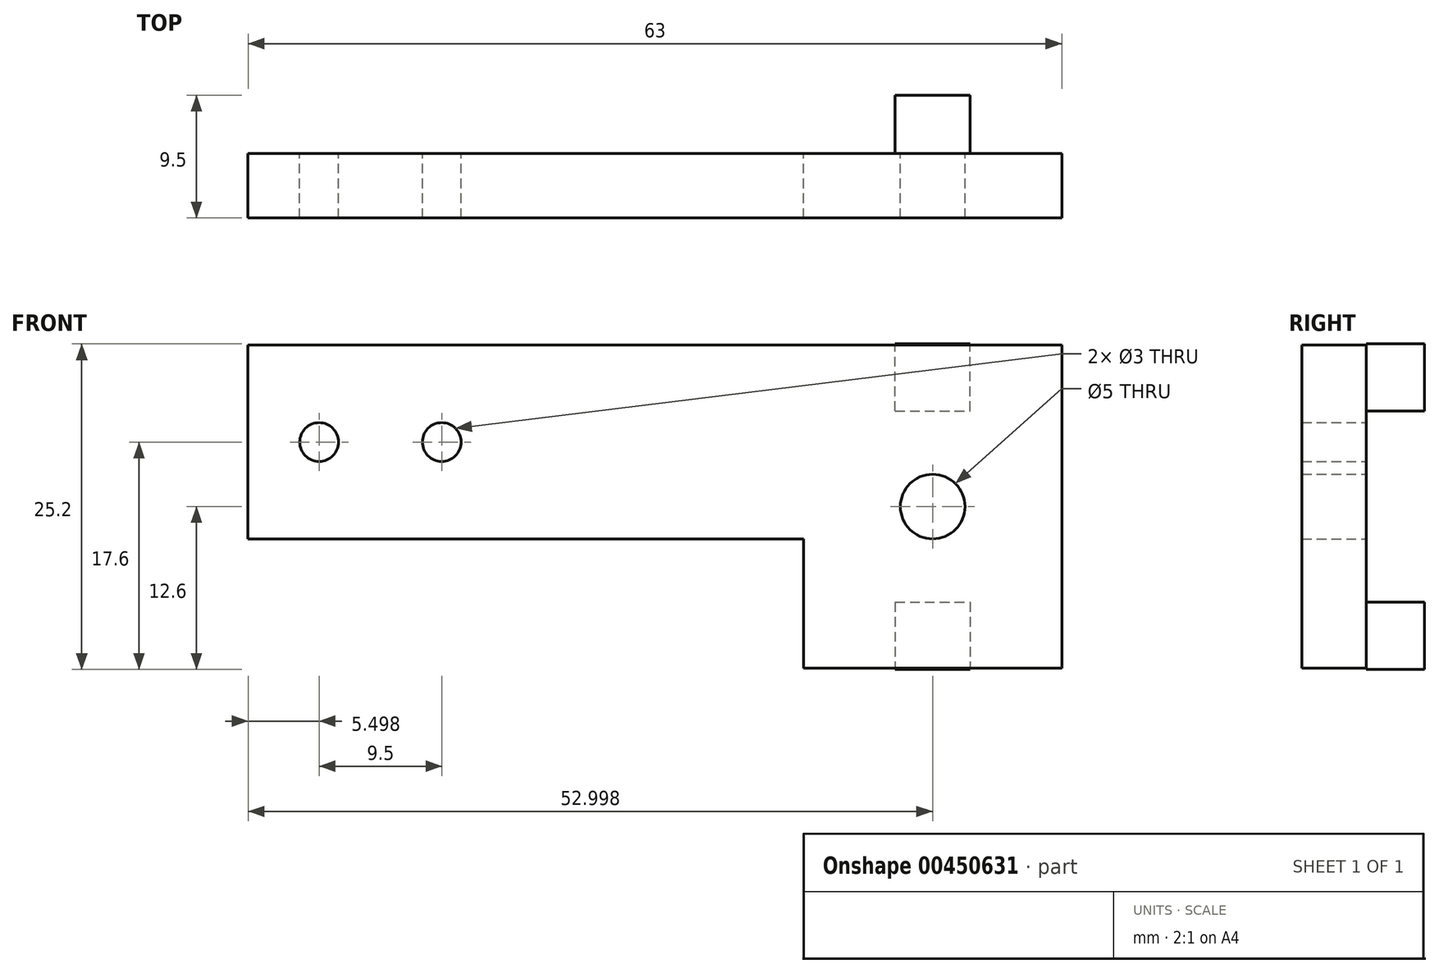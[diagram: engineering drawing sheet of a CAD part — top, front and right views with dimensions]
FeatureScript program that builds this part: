
annotation { "Feature Type Name" : "Feature", "Feature Type Description" : "" }
export const myFeature = defineFeature(function(context is Context, id is Id, definition is map)
    precondition{}
    {
        {
            var Q0;
            Q0=qCreatedBy(makeId("Front.planeOp"),FACE);
            var sketch = newSketch(context, id + "F0", { "sketchPlane" : qUnion([Q0])});
            skLineSegment(sketch, "E0.bottom", {"start": v(34.4, 12.5) * mm, "end": v(14.4, 12.5) * mm});
            skLineSegment(sketch, "E0.top", {"start": v(34.4, -12.5) * mm, "end": v(14.4, -12.5) * mm});
            skLineSegment(sketch, "E0.left", {"start": v(34.4, 12.5) * mm, "end": v(34.4, -12.5) * mm});
            skLineSegment(sketch, "E0.right", {"start": v(14.4, -2.5) * mm, "end": v(14.4, -12.5) * mm});
            skPoint(sketch, "E0.middle", {"position": v(24.4, 0) * mm});
            skLineSegment(sketch, "E1", {"start": v(14.4, 12.5) * mm, "end": v(-28.6, 12.5) * mm});
            skLineSegment(sketch, "E2", {"start": v(14.4, -2.5) * mm, "end": v(-28.6, -2.5) * mm});
            skLineSegment(sketch, "E3", {"start": v(-28.6, 12.5) * mm, "end": v(-28.6, -2.5) * mm});
            skCircle(sketch, "E4", {"center": v(24.4, 0) * mm, "radius": 2.5 * mm});
            skLineSegment(sketch, "E5", {"start": v(-28.6, 5) * mm, "end": v(-6.2, 5) * mm, "construction": true});
            skCircle(sketch, "E6", {"center": v(-13.6, 5) * mm, "radius": 1.5 * mm});
            skPoint(sketch, "E7", {"position": v(-23.1, 12.5) * mm});
            skPoint(sketch, "E8", {"position": v(-28.6, 12.5) * mm});
            skCircle(sketch, "E9", {"center": v(-23.1, 5) * mm, "radius": 1.5 * mm});
            skSolve(sketch);
        }
        {
            var Q0;
            Q0 = qSketchRegion(id + "F0", true);
            extrude(context, id + "F1", {"entities" : qUnion([Q0]), "depth" : 5 * mm});
        }
        {
            var Q0;
            Q0=makeQuery(id+"F1.opExtrude","CAP_FACE",FACE,{"disambiguationData":[OSD([sQuery(id+"F0.wireOp",EDGE,"E0.bottom"),sQuery(id+"F0.wireOp",EDGE,"E0.top"),sQuery(id+"F0.wireOp",EDGE,"E0.left"),sQuery(id+"F0.wireOp",EDGE,"E0.right"),sQuery(id+"F0.wireOp",EDGE,"E1"),sQuery(id+"F0.wireOp",EDGE,"E2"),sQuery(id+"F0.wireOp",EDGE,"E3"),sQuery(id+"F0.wireOp",EDGE,"E4"),sQuery(id+"F0.wireOp",EDGE,"E6"),sQuery(id+"F0.wireOp",EDGE,"E9")])],"isStart":true});
            cPlane(context, id + "F2", {"entities" : qUnion([Q0]), "cplaneType" : CPlaneType.OFFSET, "offset" : 0 * mm, "width" : 150 * mm, "height" : 150 * mm});
        }
        {
            var Q0;
            Q0=qCreatedBy(id+"F2.planeOp",FACE);
            var sketch = newSketch(context, id + "F3", { "sketchPlane" : qUnion([Q0])});
            skCircle(sketch, "E10.0", {"center": v(-24.4, 0) * mm, "radius": 2.5 * mm, "construction": true});
            skLineSegment(sketch, "E11", {"start": v(-24.4, 12.6) * mm, "end": v(-24.4, -13.63) * mm, "construction": true});
            skLineSegment(sketch, "E12.bottom", {"start": v(-21.5, 7.4) * mm, "end": v(-27.3, 7.4) * mm});
            skLineSegment(sketch, "E12.left", {"start": v(-21.5, 7.4) * mm, "end": v(-21.5, 12.6) * mm});
            skLineSegment(sketch, "E12.right", {"start": v(-27.3, 7.4) * mm, "end": v(-27.3, 12.6) * mm});
            skPoint(sketch, "E13", {"position": v(-21.5, 12.6) * mm});
            skPoint(sketch, "E14", {"position": v(-27.3, 12.6) * mm});
            skLineSegment(sketch, "E15", {"start": v(-21.5, 12.6) * mm, "end": v(-27.3, 12.6) * mm});
            skLineSegment(sketch, "E16", {"start": v(-3.15, 0) * mm, "end": v(-41.19, 0) * mm, "construction": true});
            skLineSegment(sketch, "E17.MirrorCS", {"start": v(-21.5, -7.4) * mm, "end": v(-21.5, -12.6) * mm});
            skLineSegment(sketch, "E18.MirrorCS", {"start": v(-21.5, -12.6) * mm, "end": v(-27.3, -12.6) * mm});
            skLineSegment(sketch, "E19.MirrorCS", {"start": v(-27.3, -7.4) * mm, "end": v(-27.3, -12.6) * mm});
            skLineSegment(sketch, "E20.MirrorCS", {"start": v(-21.5, -7.4) * mm, "end": v(-27.3, -7.4) * mm});
            skSolve(sketch);
        }
        {
            var Q0;
            Q0=makeQuery(id+"F3.imprint","IMPRINT",FACE,{"disambiguationData":[TD([[makeQuery(id+"F3.imprint","IMPRINT",EDGE,{"derivedFrom":sQuery(id+"F3.wireOp",EDGE,"E12.bottom")}),-1.0]])]});
            var Q1;
            Q1=makeQuery(id+"F3.imprint","IMPRINT",FACE,{"disambiguationData":[TD([[makeQuery(id+"F3.imprint","IMPRINT",EDGE,{"derivedFrom":sQuery(id+"F3.wireOp",EDGE,"E17.MirrorCS")}),-1.0]])]});
            extrude(context, id + "F4", {"entities" : qUnion([Q0, Q1]), "operationType" : NewBodyOperationType.ADD, "depth" : 4.5 * mm});
        }
    });
